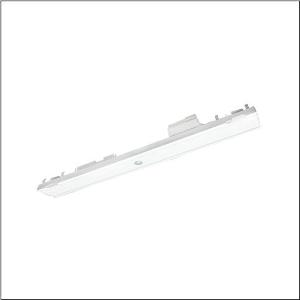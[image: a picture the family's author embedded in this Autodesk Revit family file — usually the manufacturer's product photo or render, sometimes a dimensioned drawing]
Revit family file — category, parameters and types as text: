
# Revit family: licross_r_56tl197c4x31_8620
name_source: partatom
category: Lighting Fixtures
units: mm (PartAtom-declared; Revit-internal decimal feet)

## family parameters
Cut with Voids When Loaded = No
Host = Face
Light Source = No
Part Type = Normal
Room Calculation Point = No
Round Connector Dimension = Use Diameter
Shared = No

## types (1)
- Licross® (1 x LED, 300 lm, 3.9 W, 4000K)
    Apparent Load = 4 VA
    CIE Flux Codes = 25 51 93 100 100
    Color Rendering = 70
    Color Temperature = 4000K
    Default Elevation = 1800 mm
    Description = Licross®, luminaire insert, of sheet steel, coil coated, white, length: 500mm, width: 59mm, height: 60mm, mounting height: 2.5..7m, emergency light element,LED rated luminous flux: 300lm, light colour: 740, control gear: CEAG, with plug, 6-pole, with phase selection, mains connection: 220..240V, AC/DC, 0/50..60Hz, rated input power: 3.9W, halogen-free wiring, for trunking rail, 9..14-pole, for emergency light function, supply monitoring module CEAG, with address switch, choice between two emergency light lines via tool-free moving of contact pin prior to installation in trunking rail, primary light control with lens, of PMMA, primary optical cover: cover, of PMMA, light emission: direct distribution, primary light characteristic: asymmetric,  for escape and rescue routes, compatible with all CEAG STAR technology systems (ZB-S, DG-S (DualGuard-S), LP-STAR, AT-S+), protection rating (complete): IP40, insulation class (complete): insulation class I (protective earthing), certification: CE, UKCA, protection symbol: D if used in an environment without relevant dust loads, impact resistance: IK06, permissible ambient temperature for indoor applications: -20..+40°C, packaging unit: 1 piece
    Height = 60 mm  [stored 0.19685 ft]
    Lamp = 1 x LED
    Lamp Light Flux = 300 lm
    Lamp Power = 3.9 W
    Lamp count = 1
    Length = 500 mm
    Luminous efficacy = 77 lm/W
    Manufacturer = Siteco
    ModVariant = No
    Model = 56TL197C4X31
    Mounting Place = Ceiling
    Mounting Type = Pendant
    Number of Poles = 1
    OnlyDefault = Yes
    Power Factor = 1
    Product Name = Licross®
    Product group = luminaire insert
    ProductGroupID = 901
    Protection Class = Protection class I
    Protection Degree = IP 40
    RLX_Detail_Level = 1
    RLX_Emergency_Light_Flux = 0 lm
    RLX_Emergency_Type = 0
    RLX_Emergency_Type_DB = No
    RlxData = <blob elided: 29001 chars, md5=700ebb06>
    Socket = socket
    Standby Power = 0 W
    System Light Flux = 300 lm
    System Power = 4 W
    Type Comments = Product without accessories
    Type Image = l_1251804.jpg
    URL = http://relux.com
    VarID = ---
    Voltage = 0 V
    Weight = 0.00 kg
    Width = 59 mm

note: [stored X ft] marks values corroborated as IEEE doubles in the binary element streams (Revit-internal decimal feet)

## geometry (parser evidence)
native form markers: Blend x4, Sweep x8
no freeform markers — native parametric forms only
